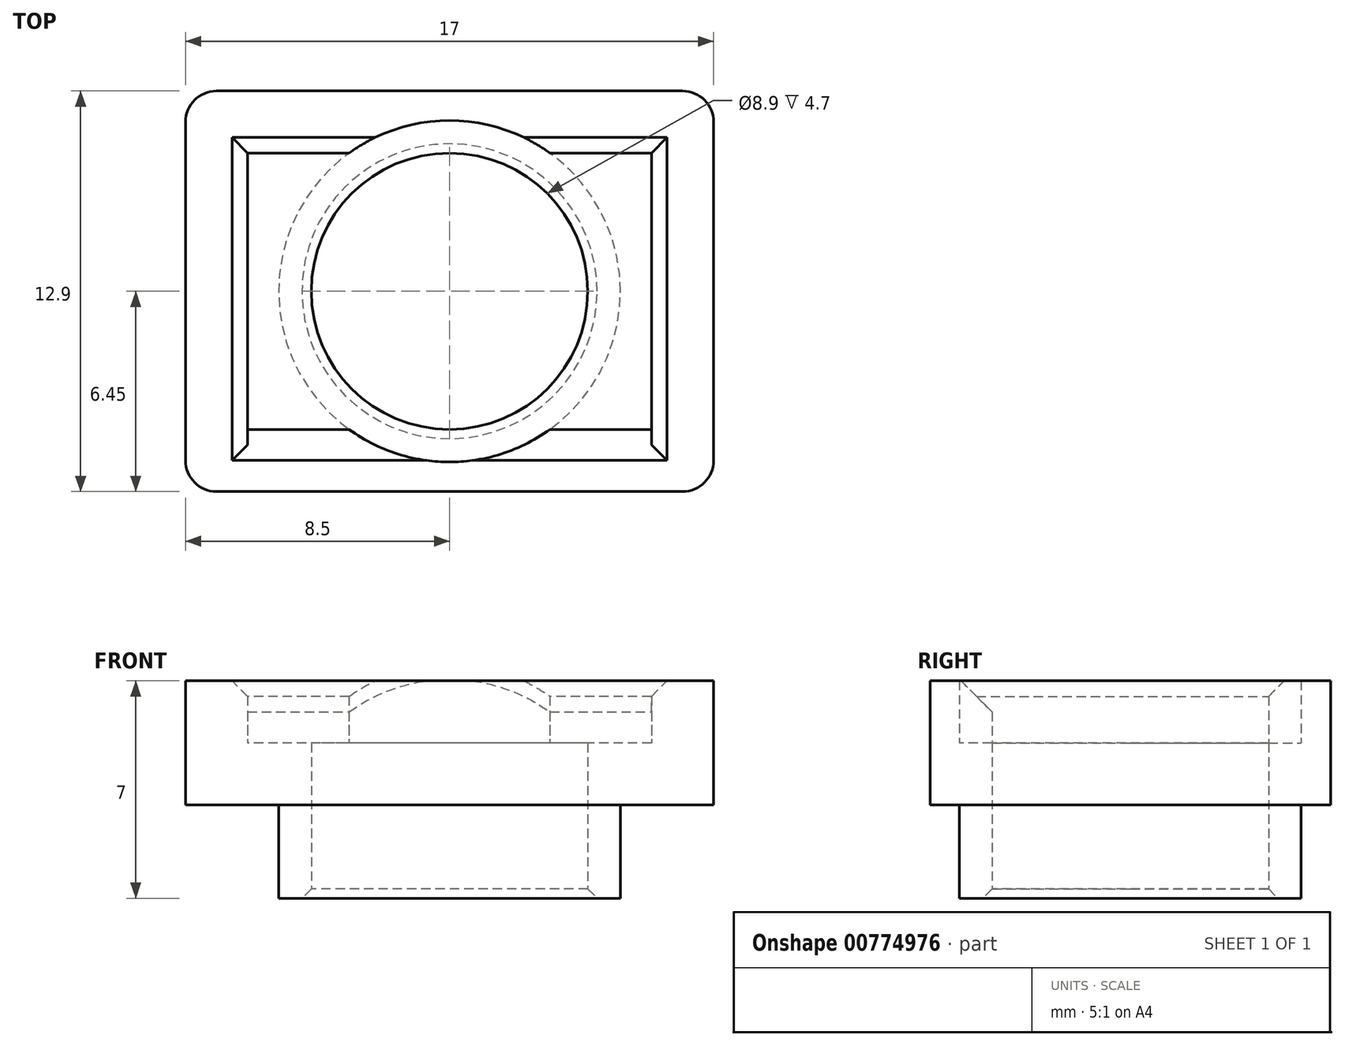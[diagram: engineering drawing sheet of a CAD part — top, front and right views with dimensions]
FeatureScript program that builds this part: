
annotation { "Feature Type Name" : "Feature", "Feature Type Description" : "" }
export const myFeature = defineFeature(function(context is Context, id is Id, definition is map)
    precondition{}
    {
        {
            var Q0;
            Q0=qCreatedBy(makeId("Top.planeOp"),FACE);
            var sketch = newSketch(context, id + "F0", { "sketchPlane" : qUnion([Q0])});
            skCircle(sketch, "E0", {"center": v(0, 0) * mm, "radius": 4.45 * mm});
            skCircle(sketch, "E1", {"center": v(0, 0) * mm, "radius": 5.5 * mm});
            skSolve(sketch);
        }
        {
            var Q0;
            Q0=makeQuery(id+"F0.imprint","IMPRINT",FACE,{"disambiguationData":[TD([[makeQuery(id+"F0.imprint","IMPRINT",EDGE,{"derivedFrom":sQuery(id+"F0.wireOp",EDGE,"E0")}),-1.0]])]});
            extrude(context, id + "F1", {"entities" : qUnion([Q0]), "depth" : 5 * mm, "offsetDistance" : 25 * mm});
        }
        {
            var Q0;
            Q0=makeQuery(id+"F1.opExtrude","CAP_FACE",FACE,{"disambiguationData":[OSD([sQuery(id+"F0.wireOp",EDGE,"E0"),sQuery(id+"F0.wireOp",EDGE,"E1")])],"isStart":false});
            var sketch = newSketch(context, id + "F2", { "sketchPlane" : qUnion([Q0])});
            skLineSegment(sketch, "E2.bottom", {"start": v(6.5, -4.45) * mm, "end": v(-6.5, -4.45) * mm});
            skLineSegment(sketch, "E2.top", {"start": v(6.5, 4.45) * mm, "end": v(-6.5, 4.45) * mm});
            skLineSegment(sketch, "E2.left", {"start": v(6.5, -4.45) * mm, "end": v(6.5, 4.45) * mm});
            skLineSegment(sketch, "E2.right", {"start": v(-6.5, -4.45) * mm, "end": v(-6.5, 4.45) * mm});
            skPoint(sketch, "E2.middle", {"position": v(0, 0) * mm});
            skLineSegment(sketch, "E3.0", {"start": v(8.5, 6.45) * mm, "end": v(-8.5, 6.45) * mm});
            skLineSegment(sketch, "E3.1", {"start": v(8.5, -6.45) * mm, "end": v(8.5, 6.45) * mm});
            skLineSegment(sketch, "E3.2", {"start": v(8.5, -6.45) * mm, "end": v(-8.5, -6.45) * mm});
            skLineSegment(sketch, "E3.3", {"start": v(-8.5, -6.45) * mm, "end": v(-8.5, 6.45) * mm});
            skLineSegment(sketch, "E4", {"start": v(-6.5, -4.45) * mm, "end": v(-6.5, -6.45) * mm});
            skLineSegment(sketch, "E5", {"start": v(6.5, -4.45) * mm, "end": v(6.5, -6.45) * mm});
            skSolve(sketch);
        }
        {
            var Q0;
            {var subQ0=sQuery(id+"F2.wireOp",EDGE,"E2.bottom");var subQ1=makeQuery(id+"F1.opExtrude","CAP_EDGE",EDGE,{"disambiguationData":[OSD([sQuery(id+"F0.wireOp",EDGE,"E0")])],"isStart":false});var subQ2=makeQuery(id+"F2.imprint","INTERSECT",VERTEX,{"derivedFrom":[subQ1,subQ0]});Q0=makeQuery(id+"F2.imprint","IMPRINT",FACE,{"disambiguationData":[TD([[makeQuery(id+"F2.imprint","IMPRINT",EDGE,{"disambiguationData":[TD([[subQ2,-1.0]])],"derivedFrom":subQ0}),-1.0]])]});}
            var Q1;
            {var subQ0=sQuery(id+"F2.wireOp",EDGE,"E2.bottom");var subQ1=makeQuery(id+"F1.opExtrude","CAP_EDGE",EDGE,{"disambiguationData":[OSD([sQuery(id+"F0.wireOp",EDGE,"E1")])],"isStart":false});var subQ2=makeQuery(id+"F2.imprint","INTERSECT",VERTEX,{"disambiguationData":[OD(0.0)],"derivedFrom":[subQ1,subQ0]});Q1=makeQuery(id+"F2.imprint","IMPRINT",FACE,{"disambiguationData":[TD([[makeQuery(id+"F2.imprint","IMPRINT",EDGE,{"disambiguationData":[TD([[subQ2,-1.0]])],"derivedFrom":subQ0}),-1.0]])]});}
            var Q2;
            {var subQ0=sQuery(id+"F2.wireOp",EDGE,"E2.right");Q2=makeQuery(id+"F2.imprint","IMPRINT",FACE,{"disambiguationData":[TD([[makeQuery(id+"F2.imprint","IMPRINT",EDGE,{"derivedFrom":subQ0}),-1.0]])]});}
            var Q3;
            {var subQ0=sQuery(id+"F2.wireOp",EDGE,"E2.left");Q3=makeQuery(id+"F2.imprint","IMPRINT",FACE,{"disambiguationData":[TD([[makeQuery(id+"F2.imprint","IMPRINT",EDGE,{"derivedFrom":subQ0}),1.0]])]});}
            extrude(context, id + "F3", {"entities" : qUnion([Q0, Q1, Q2, Q3]), "operationType" : NewBodyOperationType.ADD, "oppositeDirection" : true, "depth" : 2 * mm, "offsetDistance" : 25 * mm});
        }
        {
            var Q0;
            {var subQ5=sQuery(id+"F2.wireOp",EDGE,"E2.left");Q0=makeQuery(id+"F2.imprint","IMPRINT",FACE,{"disambiguationData":[TD([[makeQuery(id+"F2.imprint","IMPRINT",EDGE,{"derivedFrom":subQ5}),-1.0]])]});}
            var Q1;
            {var subQ0=sQuery(id+"F2.wireOp",EDGE,"E4");Q1=makeQuery(id+"F2.imprint","IMPRINT",FACE,{"disambiguationData":[TD([[makeQuery(id+"F2.imprint","IMPRINT",EDGE,{"derivedFrom":subQ0}),1.0]])]});}
            extrude(context, id + "F4", {"entities" : qUnion([Q0, Q1]), "operationType" : NewBodyOperationType.ADD, "endBound" : BoundingType.SYMMETRIC, "depth" : 4 * mm, "offsetDistance" : 25 * mm});
        }
        {
            var Q0;
            {var subQ0=sQuery(id+"F2.wireOp",EDGE,"E2.bottom");Q0=makeQuery(id+"F4.opExtrude","CAP_EDGE",EDGE,{"disambiguationData":[OSD([subQ0]),TDD([makeQuery(id+"F2.imprint","IMPRINT",EDGE,{"disambiguationData":[TD([[makeQuery(id+"F2.imprint","INTERSECT",VERTEX,{"disambiguationData":[OD(1.0)],"derivedFrom":[makeQuery(id+"F1.opExtrude","CAP_EDGE",EDGE,{"disambiguationData":[OSD([sQuery(id+"F0.wireOp",EDGE,"E1")])],"isStart":false}),subQ0]}),-1.0]])],"derivedFrom":subQ0})])],"isStart":false});}
            var Q1;
            {var subQ0=sQuery(id+"F2.wireOp",EDGE,"E2.bottom");Q1=makeQuery(id+"F4.opExtrude","CAP_EDGE",EDGE,{"disambiguationData":[OSD([subQ0]),TDD([makeQuery(id+"F2.imprint","IMPRINT",EDGE,{"disambiguationData":[TD([[makeQuery(id+"F2.imprint","INTERSECT",VERTEX,{"disambiguationData":[OD(0.0)],"derivedFrom":[makeQuery(id+"F1.opExtrude","CAP_EDGE",EDGE,{"disambiguationData":[OSD([sQuery(id+"F0.wireOp",EDGE,"E1")])],"isStart":false}),subQ0]}),1.0]])],"derivedFrom":subQ0})])],"isStart":false});}
            chamfer(context, id + "F5", {"entities" : qUnion([Q0, Q1]), "width" : 1 * mm, "tangentPropagation" : true});
        }
        {
            var Q0;
            {var subQ0=sQuery(id+"F2.wireOp",EDGE,"E2.top");Q0=makeQuery(id+"F4.opExtrude","CAP_EDGE",EDGE,{"disambiguationData":[OSD([subQ0]),TDD([makeQuery(id+"F2.imprint","IMPRINT",EDGE,{"disambiguationData":[TD([[makeQuery(id+"F2.imprint","INTERSECT",VERTEX,{"derivedFrom":[subQ0,sQuery(id+"F2.wireOp",EDGE,"E2.right")]}),1.0]])],"derivedFrom":subQ0})])],"isStart":false});}
            var Q1;
            Q1=makeQuery(id+"F4.opExtrude","CAP_EDGE",EDGE,{"disambiguationData":[OSD([sQuery(id+"F2.wireOp",EDGE,"E2.right")])],"isStart":false});
            var Q2;
            Q2=makeQuery(id+"F4.opExtrude","CAP_EDGE",EDGE,{"disambiguationData":[OSD([sQuery(id+"F2.wireOp",EDGE,"E2.left")])],"isStart":false});
            var Q3;
            {var subQ0=sQuery(id+"F2.wireOp",EDGE,"E2.top");Q3=makeQuery(id+"F4.opExtrude","CAP_EDGE",EDGE,{"disambiguationData":[OSD([subQ0]),TDD([makeQuery(id+"F2.imprint","IMPRINT",EDGE,{"disambiguationData":[TD([[makeQuery(id+"F2.imprint","INTERSECT",VERTEX,{"derivedFrom":[subQ0,sQuery(id+"F2.wireOp",EDGE,"E2.left")]}),-1.0]])],"derivedFrom":subQ0})])],"isStart":false});}
            chamfer(context, id + "F6", {"entities" : qUnion([Q0, Q1, Q2, Q3]), "width" : 0.5 * mm, "tangentPropagation" : true});
        }
        {
            var Q0;
            Q0=makeQuery(id+"F1.opExtrude","CAP_EDGE",EDGE,{"disambiguationData":[OSD([sQuery(id+"F0.wireOp",EDGE,"E0")])],"isStart":true});
            chamfer(context, id + "F7", {"entities" : qUnion([Q0]), "width" : 0.3 * mm, "tangentPropagation" : true});
        }
        {
            var Q0;
            Q0=makeQuery(id+"F4.opExtrude","SWEPT_EDGE",EDGE,{"disambiguationData":[OSD([sQuery(id+"F2.wireOp",EDGE,"E3.2"),sQuery(id+"F2.wireOp",EDGE,"E3.3")])]});
            var Q1;
            Q1=makeQuery(id+"F4.opExtrude","SWEPT_EDGE",EDGE,{"disambiguationData":[OSD([sQuery(id+"F2.wireOp",EDGE,"E3.1"),sQuery(id+"F2.wireOp",EDGE,"E3.2")])]});
            var Q2;
            Q2=makeQuery(id+"F4.opExtrude","SWEPT_EDGE",EDGE,{"disambiguationData":[OSD([sQuery(id+"F2.wireOp",EDGE,"E3.0"),sQuery(id+"F2.wireOp",EDGE,"E3.1")])]});
            var Q3;
            Q3=makeQuery(id+"F4.opExtrude","SWEPT_EDGE",EDGE,{"disambiguationData":[OSD([sQuery(id+"F2.wireOp",EDGE,"E3.0"),sQuery(id+"F2.wireOp",EDGE,"E3.3")])]});
            fillet(context, id + "F8", {"entities" : qUnion([Q0, Q1, Q2, Q3]), "radius" : 1 * mm, "tangentPropagation" : true, "allowEdgeOverflow" : false});
        }
    });
